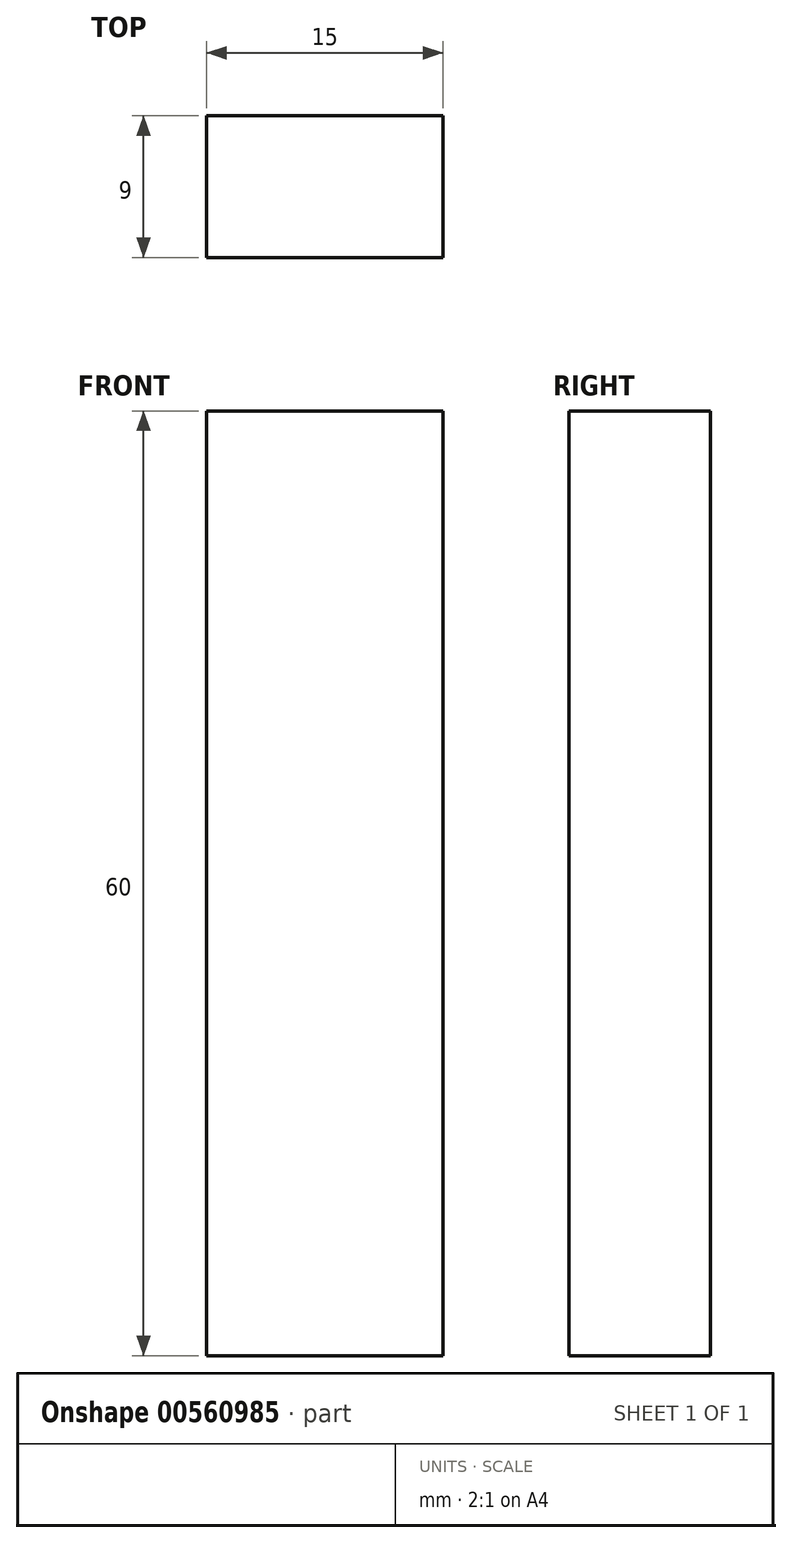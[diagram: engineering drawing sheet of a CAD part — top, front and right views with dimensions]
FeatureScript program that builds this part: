
annotation { "Feature Type Name" : "Feature", "Feature Type Description" : "" }
export const myFeature = defineFeature(function(context is Context, id is Id, definition is map)
    precondition{}
    {
        {
            var Q0;
            Q0=qCreatedBy(makeId("Top.planeOp"),FACE);
            var sketch = newSketch(context, id + "F0", { "sketchPlane" : qUnion([Q0])});
            skLineSegment(sketch, "E0.bottom", {"start": v(7.5, -4.5) * mm, "end": v(-7.5, -4.5) * mm});
            skLineSegment(sketch, "E0.top", {"start": v(7.5, 4.5) * mm, "end": v(-7.5, 4.5) * mm});
            skLineSegment(sketch, "E0.left", {"start": v(7.5, -4.5) * mm, "end": v(7.5, 4.5) * mm});
            skLineSegment(sketch, "E0.right", {"start": v(-7.5, -4.5) * mm, "end": v(-7.5, 4.5) * mm});
            skPoint(sketch, "E0.middle", {"position": v(0, 0) * mm});
            skSolve(sketch);
        }
        {
            var Q0;
            Q0=qSketchRegion(id+"F0",true);
            extrude(context, id + "F1", {"entities" : qUnion([Q0]), "endBound" : BoundingType.SYMMETRIC, "depth" : 60 * mm});
        }
    });
